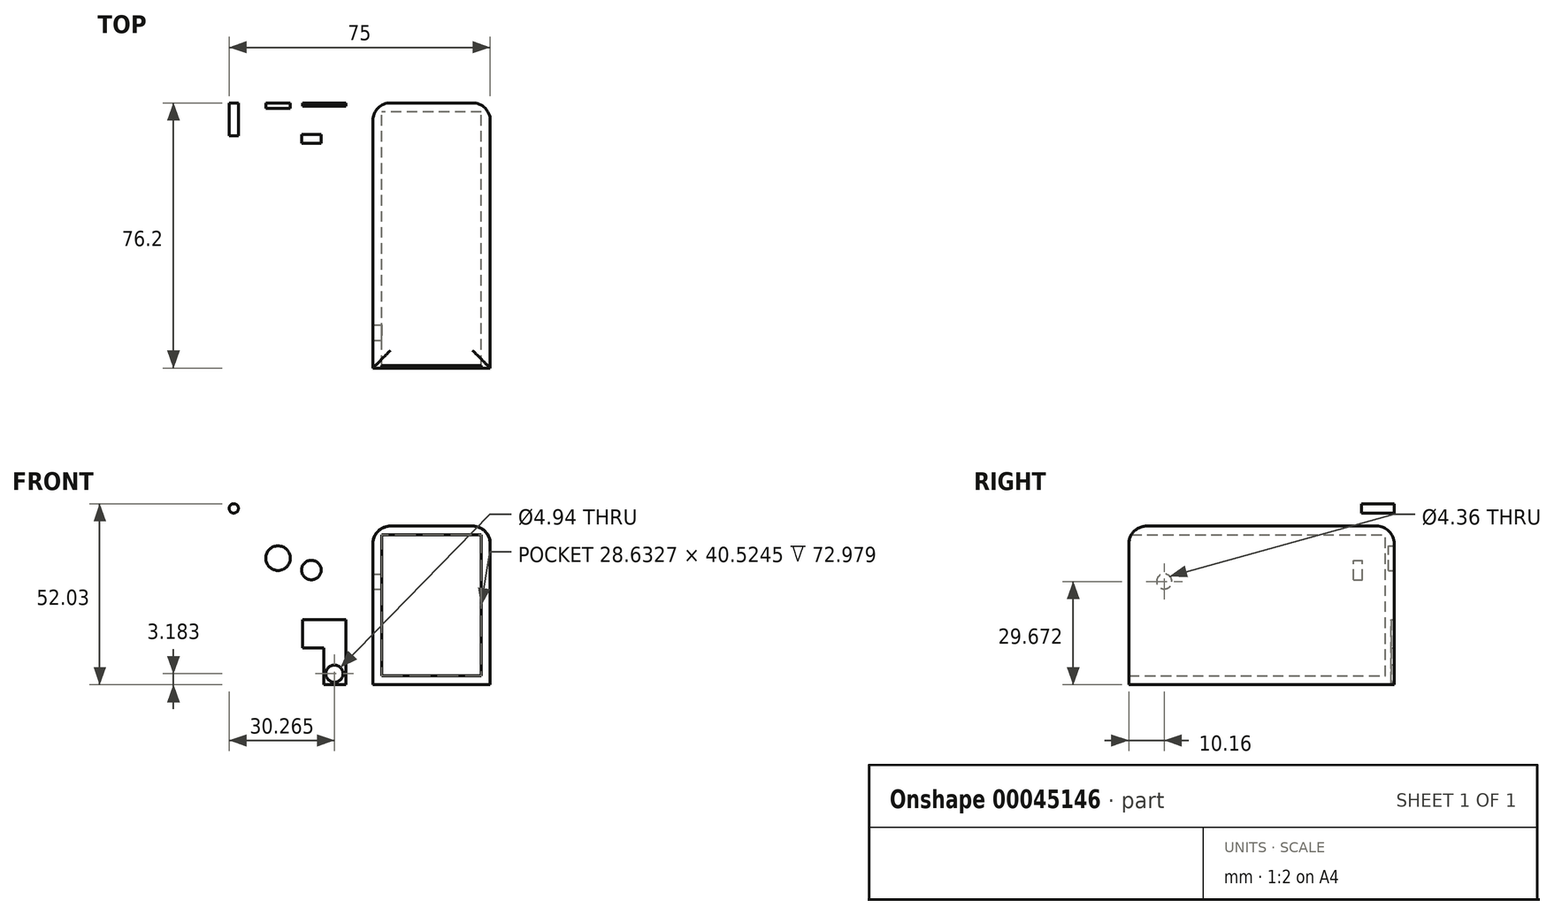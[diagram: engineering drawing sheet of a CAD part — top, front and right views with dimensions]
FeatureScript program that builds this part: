
annotation { "Feature Type Name" : "Feature", "Feature Type Description" : "" }
export const myFeature = defineFeature(function(context is Context, id is Id, definition is map)
    precondition{}
    {
        {
            var Q0;
            Q0=qCreatedBy(makeId("Front.planeOp"),FACE);
            var sketch = newSketch(context, id + "F0", { "sketchPlane" : qUnion([Q0])});
            skLineSegment(sketch, "E0", {"start": v(0, 0) * mm, "end": v(0, 45.6) * mm});
            skLineSegment(sketch, "E1", {"start": v(0, 45.6) * mm, "end": v(33.71, 45.6) * mm});
            skLineSegment(sketch, "E2", {"start": v(33.71, 45.6) * mm, "end": v(33.71, 0) * mm});
            skLineSegment(sketch, "E3", {"start": v(33.71, 0) * mm, "end": v(0, 0) * mm});
            skSolve(sketch);
        }
        {
            var Q0;
            Q0=makeQuery(id+"F0.imprint","IMPRINT",FACE,{"disambiguationData":[TD([[makeQuery(id+"F0.imprint","IMPRINT",EDGE,{"derivedFrom":sQuery(id+"F0.wireOp",EDGE,"E0")}),-1.0]])]});
            extrude(context, id + "F1", {"entities" : qUnion([Q0]), "depth" : 76.2 * mm});
        }
        {
            var Q0;
            Q0=makeQuery(id+"F1.opExtrude","CAP_FACE",FACE,{"disambiguationData":[OSD([sQuery(id+"F0.wireOp",EDGE,"E0"),sQuery(id+"F0.wireOp",EDGE,"E1"),sQuery(id+"F0.wireOp",EDGE,"E2"),sQuery(id+"F0.wireOp",EDGE,"E3")])],"isStart":false});
            shell(context, id + "F2", {"entities" : qUnion([Q0]), "thickness" : 2.54 * mm});
        }
        {
            var Q0;
            Q0=makeQuery(id+"F1.opExtrude","SWEPT_FACE",FACE,{"disambiguationData":[OSD([sQuery(id+"F0.wireOp",EDGE,"E1")])]});
            var Q1;
            Q1=makeQuery(id+"F1.opExtrude","CAP_EDGE",EDGE,{"disambiguationData":[OSD([sQuery(id+"F0.wireOp",EDGE,"E0")])],"isStart":true});
            var Q2;
            Q2=makeQuery(id+"F1.opExtrude","CAP_EDGE",EDGE,{"disambiguationData":[OSD([sQuery(id+"F0.wireOp",EDGE,"E2")])],"isStart":true});
            fillet(context, id + "F3", {"entities" : qUnion([Q0, Q1, Q2]), "radius" : 5.08 * mm, "tangentPropagation" : true, "allowEdgeOverflow" : false});
        }
        {
            var Q0;
            Q0=qCreatedBy(makeId("Front.planeOp"),FACE);
            var sketch = newSketch(context, id + "F4", { "sketchPlane" : qUnion([Q0])});
            skLineSegment(sketch, "E4", {"start": v(-10.75, 0) * mm, "end": v(-10.75, 23.32) * mm});
            skLineSegment(sketch, "E5", {"start": v(-10.75, 23.32) * mm, "end": v(-21.56, 23.32) * mm});
            skLineSegment(sketch, "E6", {"start": v(-21.56, 23.32) * mm, "end": v(-21.56, 17.04) * mm});
            skLineSegment(sketch, "E7", {"start": v(-21.56, 17.04) * mm, "end": v(-14.59, 17.04) * mm});
            skLineSegment(sketch, "E8", {"start": v(-14.59, 17.04) * mm, "end": v(-14.59, 0) * mm});
            skLineSegment(sketch, "E9", {"start": v(-14.59, 0) * mm, "end": v(-10.75, 0) * mm});
            skSolve(sketch);
        }
        {
            var Q0;
            Q0=makeQuery(id+"F4.imprint","IMPRINT",FACE,{"disambiguationData":[TD([[makeQuery(id+"F4.imprint","IMPRINT",EDGE,{"derivedFrom":sQuery(id+"F4.wireOp",EDGE,"E4")}),1.0]])]});
            extrude(context, id + "F5", {"entities" : qUnion([Q0]), "depth" : 1.69 * mm});
        }
        {
            var Q0;
            Q0=qCreatedBy(makeId("Front.planeOp"),FACE);
            var sketch = newSketch(context, id + "F6", { "sketchPlane" : qUnion([Q0])});
            skCircle(sketch, "E10", {"center": v(-27.73, 9.72) * mm, "radius": 1.17 * mm});
            skSolve(sketch);
        }
        {
            var Q0;
            Q0=makeQuery(id+"F6.imprint","IMPRINT",FACE,{"disambiguationData":[TD([[makeQuery(id+"F6.imprint","IMPRINT",EDGE,{"derivedFrom":sQuery(id+"F6.wireOp",EDGE,"E10")}),1.0]])]});
            extrude(context, id + "F7", {"entities" : qUnion([Q0]), "depth" : 25.4 * mm});
        }
        {
            var Q0;
            Q0=makeQuery(id+"F7.opExtrude","SWEPT_BODY",BODY,{"disambiguationData":[OSD([sQuery(id+"F6.wireOp",EDGE,"E10")])]});
            transform(context, id + "F8", {"entities" : qUnion([Q0]), "transformType" : TransformType.TRANSLATION_3D, "dx" : 15.03 * mm, "dy" : 0 * mm, "dz" : -7.57 * mm, "makeCopy" : false});
        }
        {
            var Q0;
            Q0=makeQuery(id+"F7.opExtrude","CAP_FACE",FACE,{"disambiguationData":[OSD([sQuery(id+"F6.wireOp",EDGE,"E10")])],"isStart":false});
            extrude(context, id + "F9", {"entities" : qUnion([Q0]), "operationType" : NewBodyOperationType.REMOVE, "oppositeDirection" : true, "depth" : 39.47 * mm});
        }
        {
            var Q0;
            Q0=qCreatedBy(makeId("Right.planeOp"),FACE);
            var sketch = newSketch(context, id + "F10", { "sketchPlane" : qUnion([Q0])});
            skCircle(sketch, "E11", {"center": v(57.96, 65.23) * mm, "radius": 2.18 * mm});
            skSolve(sketch);
        }
        {
            var Q0;
            Q0=makeQuery(id+"F10.imprint","IMPRINT",FACE,{"disambiguationData":[TD([[makeQuery(id+"F10.imprint","IMPRINT",EDGE,{"derivedFrom":sQuery(id+"F10.wireOp",EDGE,"E11")}),1.0]])]});
            extrude(context, id + "F11", {"entities" : qUnion([Q0]), "depth" : 25.4 * mm});
        }
        {
            var Q0;
            Q0=makeQuery(id+"F11.opExtrude","SWEPT_BODY",BODY,{"disambiguationData":[OSD([sQuery(id+"F10.wireOp",EDGE,"E11")])]});
            transform(context, id + "F12", {"entities" : qUnion([Q0]), "transformType" : TransformType.TRANSLATION_3D, "dx" : 0 * mm, "dy" : -124 * mm, "dz" : -35.56 * mm, "makeCopy" : false});
        }
        {
            var Q0;
            Q0=makeQuery(id+"F11.opExtrude","CAP_FACE",FACE,{"disambiguationData":[OSD([sQuery(id+"F10.wireOp",EDGE,"E11")])],"isStart":false});
            extrude(context, id + "F13", {"entities" : qUnion([Q0]), "operationType" : NewBodyOperationType.REMOVE, "oppositeDirection" : true, "depth" : 52.3 * mm});
        }
        {
            var Q0;
            Q0=qCreatedBy(makeId("Front.planeOp"),FACE);
            var sketch = newSketch(context, id + "F14", { "sketchPlane" : qUnion([Q0])});
            skCircle(sketch, "E12", {"center": v(-39.95, 50.68) * mm, "radius": 1.35 * mm});
            skSolve(sketch);
        }
        {
            var Q0;
            Q0=makeQuery(id+"F14.imprint","IMPRINT",FACE,{"disambiguationData":[TD([[makeQuery(id+"F14.imprint","IMPRINT",EDGE,{"derivedFrom":sQuery(id+"F14.wireOp",EDGE,"E12")}),1.0]])]});
            extrude(context, id + "F15", {"entities" : qUnion([Q0]), "depth" : 9.4 * mm});
        }
        {
            var Q0;
            Q0=qCreatedBy(makeId("Front.planeOp"),FACE);
            var sketch = newSketch(context, id + "F16", { "sketchPlane" : qUnion([Q0])});
            skCircle(sketch, "E13", {"center": v(-58.97, 58.15) * mm, "radius": 2.81 * mm});
            skSolve(sketch);
        }
        {
            var Q0;
            Q0=makeQuery(id+"F16.imprint","IMPRINT",FACE,{"disambiguationData":[TD([[makeQuery(id+"F16.imprint","IMPRINT",EDGE,{"derivedFrom":sQuery(id+"F16.wireOp",EDGE,"E13")}),1.0]])]});
            extrude(context, id + "F17", {"entities" : qUnion([Q0]), "depth" : 2.54 * mm});
        }
        {
            var Q0;
            Q0=makeQuery(id+"F17.opExtrude","SWEPT_BODY",BODY,{"disambiguationData":[OSD([sQuery(id+"F16.wireOp",EDGE,"E13")])]});
            transform(context, id + "F18", {"entities" : qUnion([Q0]), "transformType" : TransformType.TRANSLATION_3D, "dx" : 19.1 * mm, "dy" : -9.1 * mm, "dz" : -7.55 * mm, "makeCopy" : false});
        }
        {
            var Q0;
            Q0=makeQuery(id+"F5.opExtrude","SWEPT_BODY",BODY,{"disambiguationData":[OSD([sQuery(id+"F4.wireOp",EDGE,"E4"),sQuery(id+"F4.wireOp",EDGE,"E5"),sQuery(id+"F4.wireOp",EDGE,"E6"),sQuery(id+"F4.wireOp",EDGE,"E7"),sQuery(id+"F4.wireOp",EDGE,"E8"),sQuery(id+"F4.wireOp",EDGE,"E9")])]});
            deleteBodies(context, id + "F19", {"entities" : qUnion([Q0])});
        }
        {
            var Q0;
            Q0=qCreatedBy(makeId("Front.planeOp"),FACE);
            var sketch = newSketch(context, id + "F20", { "sketchPlane" : qUnion([Q0])});
            skLineSegment(sketch, "E14", {"start": v(-7.76, 0) * mm, "end": v(-7.76, 18.7) * mm});
            skLineSegment(sketch, "E15", {"start": v(-7.76, 18.7) * mm, "end": v(-20.17, 18.7) * mm});
            skLineSegment(sketch, "E16", {"start": v(-20.17, 18.7) * mm, "end": v(-20.17, 10.53) * mm});
            skLineSegment(sketch, "E17", {"start": v(-20.17, 10.53) * mm, "end": v(-14.13, 10.53) * mm});
            skLineSegment(sketch, "E18", {"start": v(-14.13, 10.53) * mm, "end": v(-14.13, 0) * mm});
            skLineSegment(sketch, "E19", {"start": v(-14.13, 0) * mm, "end": v(-7.76, 0) * mm});
            skSolve(sketch);
        }
        {
            var Q0;
            Q0=makeQuery(id+"F20.imprint","IMPRINT",FACE,{"disambiguationData":[TD([[makeQuery(id+"F20.imprint","IMPRINT",EDGE,{"derivedFrom":sQuery(id+"F20.wireOp",EDGE,"E14")}),1.0]])]});
            extrude(context, id + "F21", {"entities" : qUnion([Q0]), "depth" : 0.9 * mm});
        }
        {
            var Q0;
            Q0=qCreatedBy(makeId("Front.planeOp"),FACE);
            var sketch = newSketch(context, id + "F22", { "sketchPlane" : qUnion([Q0])});
            skCircle(sketch, "E20", {"center": v(-40.09, 32.41) * mm, "radius": 2.47 * mm});
            skSolve(sketch);
        }
        {
            var Q0;
            Q0=makeQuery(id+"F22.imprint","IMPRINT",FACE,{"disambiguationData":[TD([[makeQuery(id+"F22.imprint","IMPRINT",EDGE,{"derivedFrom":sQuery(id+"F22.wireOp",EDGE,"E20")}),1.0]])]});
            extrude(context, id + "F23", {"entities" : qUnion([Q0]), "depth" : 25.4 * mm});
        }
        {
            var Q0;
            Q0=makeQuery(id+"F23.opExtrude","SWEPT_BODY",BODY,{"disambiguationData":[OSD([sQuery(id+"F22.wireOp",EDGE,"E20")])]});
            transform(context, id + "F24", {"entities" : qUnion([Q0]), "transformType" : TransformType.TRANSLATION_3D, "dx" : 29.06 * mm, "dy" : 0 * mm, "dz" : -29.23 * mm, "makeCopy" : false});
        }
        {
            var Q0;
            Q0=makeQuery(id+"F23.opExtrude","CAP_FACE",FACE,{"disambiguationData":[OSD([sQuery(id+"F22.wireOp",EDGE,"E20")])],"isStart":false});
            extrude(context, id + "F25", {"entities" : qUnion([Q0]), "operationType" : NewBodyOperationType.REMOVE, "oppositeDirection" : true, "depth" : 51.26 * mm});
        }
        {
            var Q0;
            Q0=makeQuery(id+"F17.opExtrude","SWEPT_BODY",BODY,{"disambiguationData":[OSD([sQuery(id+"F16.wireOp",EDGE,"E13")])]});
            transform(context, id + "F26", {"entities" : qUnion([Q0]), "transformType" : TransformType.TRANSLATION_3D, "dx" : 22.2 * mm, "dy" : 0 * mm, "dz" : -17.63 * mm, "makeCopy" : false});
        }
        {
            var Q0;
            Q0=qCreatedBy(makeId("Front.planeOp"),FACE);
            var sketch = newSketch(context, id + "F27", { "sketchPlane" : qUnion([Q0])});
            skCircle(sketch, "E21", {"center": v(-27.25, 36.37) * mm, "radius": 3.53 * mm});
            skSolve(sketch);
        }
        {
            var Q0;
            Q0=makeQuery(id+"F27.imprint","IMPRINT",FACE,{"disambiguationData":[TD([[makeQuery(id+"F27.imprint","IMPRINT",EDGE,{"derivedFrom":sQuery(id+"F27.wireOp",EDGE,"E21")}),1.0]])]});
            extrude(context, id + "F28", {"entities" : qUnion([Q0]), "depth" : 1.62 * mm});
        }
        {
            var Q0;
            Q0=qCreatedBy(makeId("Front.planeOp"),FACE);
            var sketch = newSketch(context, id + "F29", { "sketchPlane" : qUnion([Q0])});
            skLineSegment(sketch, "E22", {"start": v(-63.5, 0) * mm, "end": v(-63.5, -37.75) * mm});
            skLineSegment(sketch, "E23", {"start": v(-63.5, -37.75) * mm, "end": v(-41.33, -37.75) * mm});
            skLineSegment(sketch, "E24", {"start": v(-41.33, -37.75) * mm, "end": v(-41.33, 0) * mm});
            skLineSegment(sketch, "E25", {"start": v(-41.33, 0) * mm, "end": v(-63.5, 0) * mm});
            skSolve(sketch);
        }
        {
            var Q0;
            Q0=makeQuery(id+"F29.imprint","IMPRINT",FACE,{"disambiguationData":[TD([[makeQuery(id+"F29.imprint","IMPRINT",EDGE,{"derivedFrom":sQuery(id+"F29.wireOp",EDGE,"E22")}),1.0]])]});
            extrude(context, id + "F30", {"entities" : qUnion([Q0]), "depth" : 25.4 * mm});
        }
        {
            var Q0;
            Q0=makeQuery(id+"F30.opExtrude","SWEPT_BODY",BODY,{"disambiguationData":[OSD([sQuery(id+"F29.wireOp",EDGE,"E22"),sQuery(id+"F29.wireOp",EDGE,"E23"),sQuery(id+"F29.wireOp",EDGE,"E24"),sQuery(id+"F29.wireOp",EDGE,"E25")])]});
            deleteBodies(context, id + "F31", {"entities" : qUnion([Q0])});
        }
    });
